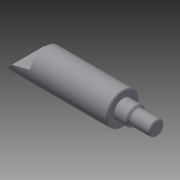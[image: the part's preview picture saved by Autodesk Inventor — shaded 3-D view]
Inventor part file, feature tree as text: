
AUTODESK INVENTOR PART (.ipt)
format: ipt  version: 2014 SP1 (Build 180222100, 222)  size: 119,296 bytes
history: native  units: in
note: dims shown in document units (in); Inventor stores cm internally (conversion verified against a paired STEP export)
features: chamfer x2, sketch x2, revolve x1, extrude x1, fillet x1, projected_geometry x1
ambient origin geometry x8: Origin, YZ Plane, XZ Plane, XY Plane, X Axis, Y Axis, Z Axis, Center Point
bodies: Solid1 (feature_tree)
feature tree (8):
  revolve  "Revolution1"  [1 undecoded]
  extrude  "Extrusion1"  TaperAngle=45.0deg  [1 undecoded]
  chamfer  "Chamfer1"  Distance=0.1085in
  fillet  "Fillet1"  Radius=0.196in
  chamfer  "Chamfer2"  Distance=0.1125in
  sketch  "Sketch1"  dims[d0=0.1875in d1=0.775in]
  sketch  "Sketch2"  dims[d2=0.085in d3=45.0deg d4=0.1085in d5=0.196in d6=0.1125in d7=90.0deg d8=45.0deg d11=0.132in d13=0.04in d14=0.074in d15=0.06in d16=1.0in d17=0.0in d18=0.005in d19=0.125in d20=45.0deg d21=0.005in d22=0.005in d23=0.125in d24=45.0deg]
  projected_geometry  "Project Cut Edges1"
note: 2 required parameter values undecoded (feature->parameter linkage not recoverable at this tier; creation-order binding heuristic only, values carry confidence <= 0.55)